# Revit family: Safety & Protection_Barrier_UltiGroup_Fixed Barrier
name_source: partatom
category: Generic Models
revit_build: Autodesk Revit Architecture 2016 (Build: 20150220_1215(x64)
units: mm (PartAtom-declared; Revit-internal decimal feet)

## family parameters
Always vertical = Yes
Can host rebar = No
Cut with Voids When Loaded = No
OmniClass Number = 23.30.80.17
OmniClass Title = Impact Protection
Part Type = Normal
Room Calculation Point = No
Round Connector Dimension = Use Diameter
Shared = No
Work Plane-Based = No

## types (5) — shared parameters
Fax = 07 846 2467
Manufacturer = UltiGroup
Send Message = http://ultigroup.co.nz
URL = http://ultigroup.co.nz
zero-valued in all types: InstallationGroup_ANZRS, ModifiedIssue_ANZRS

## per-type parameters (varying)
| type | 310-1 | 610-1 | 610-2 | 910 | 910-2 | 910-3 | Description | Model |
| 310-1 | Yes | No | No | No | No | No | Fixed Barrier System 3100mm high - Single | Ulti Fixed Barrier 310-1 |
| 610-1 | No | Yes | No | No | No | No | Fixed Barrier System 6100mm high - Single | Ulti Fixed Barrier 610-1 |
| 610-2 | No | Yes | Yes | No | No | No | Fixed Barrier System 6100mm high - Double | Ulti Fixed Barrier  610-2 |
| 910-2 | No | No | No | Yes | Yes | No | Fixed Barrier System 9100mm high - Double | Ulti Fixed Barrier 910-2 |
| 910-3 | No | No | No | Yes | No | Yes | Fixed Barrier System 9100mm high - Triple | Ulti Fixed Barrier 910-3 |

## geometry (parser evidence)
native form markers: Sweep x20
no freeform markers — native parametric forms only
